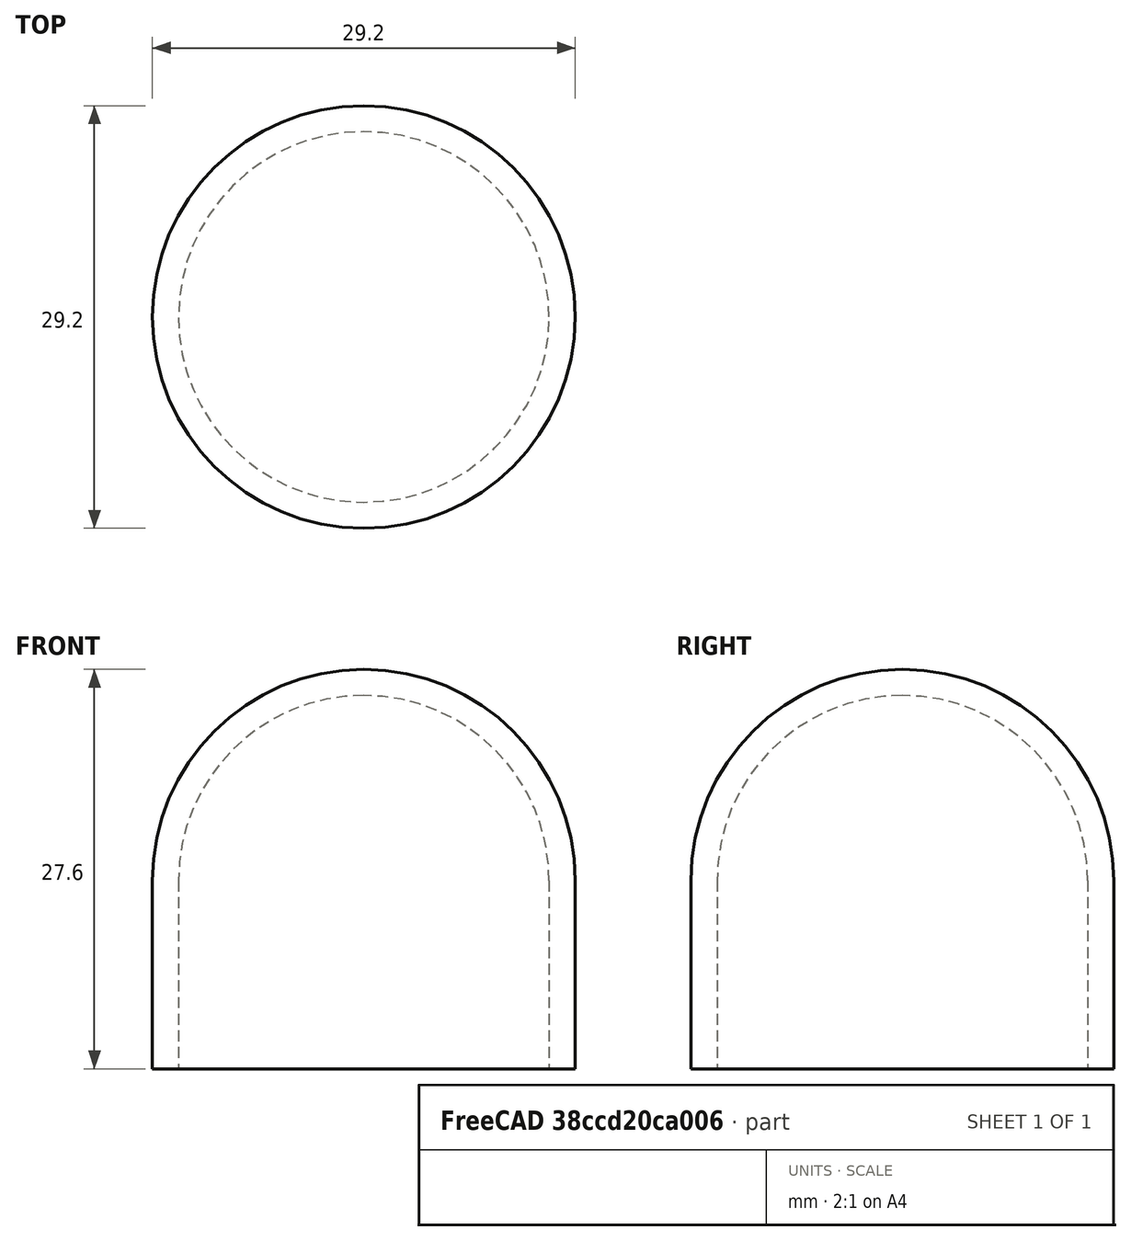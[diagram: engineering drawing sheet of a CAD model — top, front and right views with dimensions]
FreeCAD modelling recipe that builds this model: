
FCSTD DOCUMENT  (FreeCAD 0.16R)
Label: HorseyCaps
License: All rights reserved
LicenseURL: http://en.wikipedia.org/wiki/All_rights_reserved
objects: Sketcher::SketchObject×1, PartDesign::Revolution×1
note: 3 computed .brp shape members not serialized (recipe doc carries the construction recipe); baked Part::Feature solids carry a one-line shape summary decoded from their .brp

FEATURE [Sketcher::SketchObject] Sketch
  Placement = pos=(0,0,0) rot=(1,0,0;1.5708rad)
  sketch-geometry (6):
    g0: LineSegment StartX=12.8 StartY=13 StartZ=0 EndX=12.8 EndY=0 EndZ=0
    g1: LineSegment StartX=12.8 StartY=0 StartZ=0 EndX=14.6 EndY=0 EndZ=0
    g2: LineSegment StartX=14.6 StartY=0 StartZ=0 EndX=14.6 EndY=13 EndZ=0
    g3: ArcOfCircle CenterX=0 CenterY=13 CenterZ=0 NormalX=0 NormalY=0 NormalZ=1 Radius=12.8 StartAngle=6.28319 EndAngle=7.85398
    g4: ArcOfCircle CenterX=0 CenterY=13 CenterZ=0 NormalX=0 NormalY=0 NormalZ=1 Radius=14.6 StartAngle=6.28319 EndAngle=7.85398
    g5: LineSegment StartX=0 StartY=27.6 StartZ=0 EndX=0 EndY=25.8 EndZ=0
  constraints (20):
    c: Vertical(g0)
    c: Coincident(g0,g1)
    c: Horizontal(g1)
    c: Coincident(g1,g2)
    c: Vertical(g2)
    c: Coincident(g3,g0)
    c: PointOnObject(g3,g-2)
    c: Coincident(g4,g3)
    c: Coincident(g4,g2)
    c: DistanceX(g1,g1) = 1.8
    c: PointOnObject(g4,g-2)
    c: PointOnObject(g1,g-1)
    c: Vertical(g5)
    c: Coincident(g5,g4)
    c: Coincident(g5,g3)
    c: Tangent(g0,g3)
    c: Tangent(g2,g4)
    c: DistanceX(g0) = 12.8
    c: DistanceY(g2) = 13
    c: Perpendicular(g4,g-2)
FEATURE [PartDesign::Revolution] Revolution  label="Body"
  Angle = 360
  Axis = (0,0,1)
  Base = (0,0,0)
  Placement = pos=(0,0,0) rot=(1,0,0;1.5708rad)
  ReferenceAxis = -> Sketch [V_Axis]
  Reversed = true
  Sketch = -> Sketch
